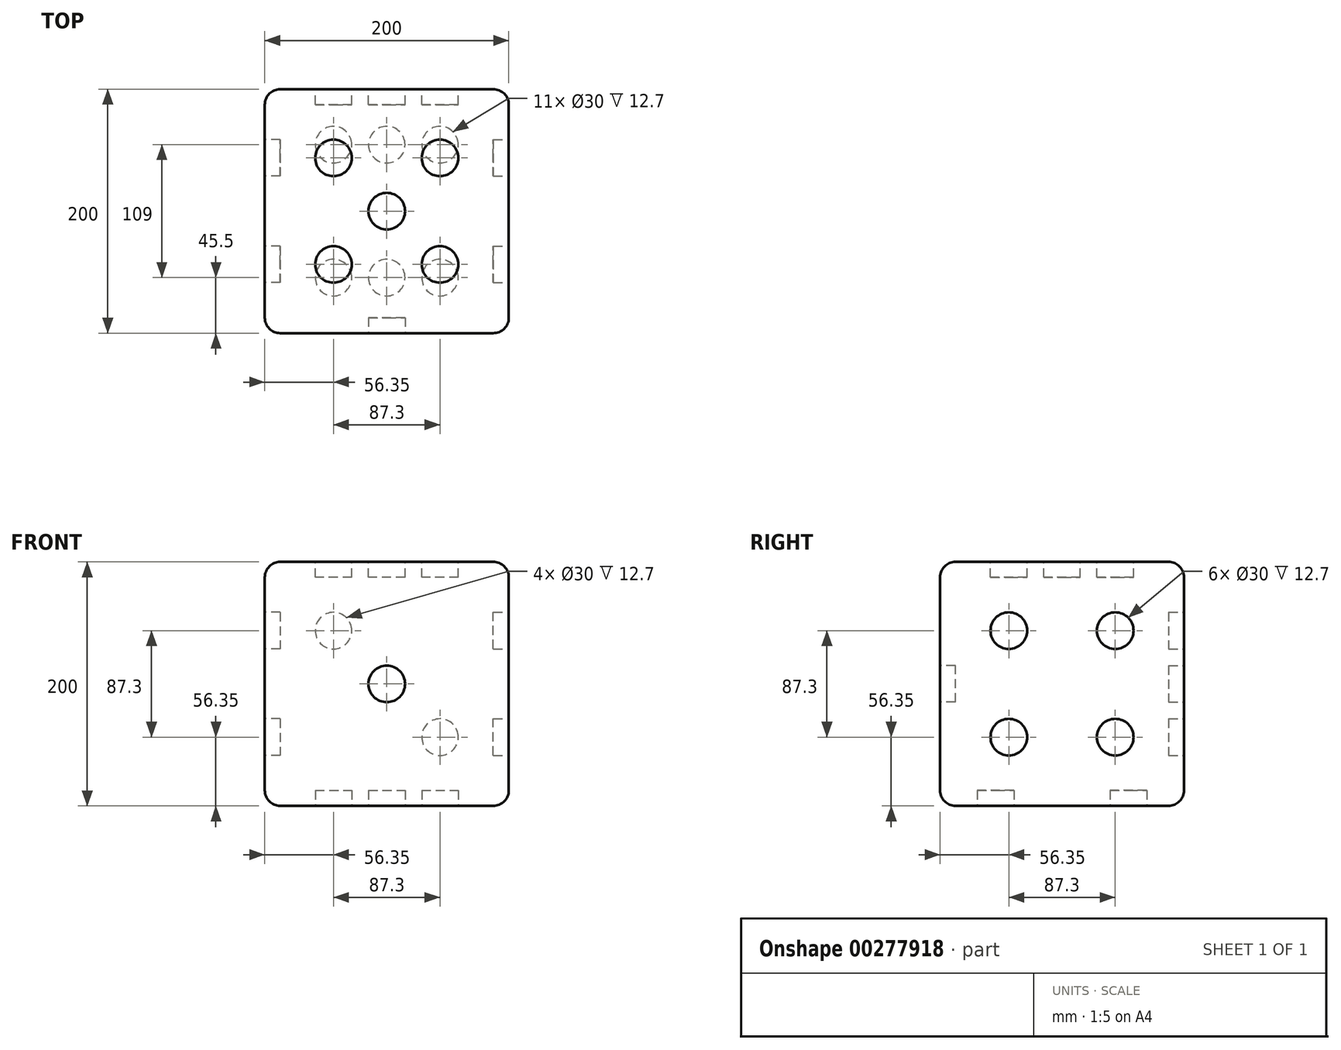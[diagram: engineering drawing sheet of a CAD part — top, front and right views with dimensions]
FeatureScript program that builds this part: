
annotation { "Feature Type Name" : "Feature", "Feature Type Description" : "" }
export const myFeature = defineFeature(function(context is Context, id is Id, definition is map)
    precondition{}
    {
        {
            var Q0;
            Q0=qCreatedBy(makeId("Front.planeOp"),FACE);
            var sketch = newSketch(context, id + "F0", { "sketchPlane" : qUnion([Q0])});
            skLineSegment(sketch, "E0.bottom", {"start": v(100, -100) * mm, "end": v(-100, -100) * mm});
            skLineSegment(sketch, "E0.top", {"start": v(100, 100) * mm, "end": v(-100, 100) * mm});
            skLineSegment(sketch, "E0.left", {"start": v(100, -100) * mm, "end": v(100, 100) * mm});
            skLineSegment(sketch, "E0.right", {"start": v(-100, -100) * mm, "end": v(-100, 100) * mm});
            skPoint(sketch, "E0.middle", {"position": v(0, 0) * mm});
            skSolve(sketch);
        }
        {
            var Q0;
            Q0 = qSketchRegion(id + "F0", true);
            extrude(context, id + "F1", {"entities" : qUnion([Q0]), "oppositeDirection" : true, "depth" : 200 * mm});
        }
        {
            var Q0;
            Q0=makeQuery(id+"F1.opExtrude","SWEPT_FACE",FACE,{"disambiguationData":[OSD([sQuery(id+"F0.wireOp",EDGE,"E0.top")])]});
            var Q1;
            Q1=makeQuery(id+"F1.opExtrude","SWEPT_FACE",FACE,{"disambiguationData":[OSD([sQuery(id+"F0.wireOp",EDGE,"E0.left")])]});
            var Q2;
            Q2=makeQuery(id+"F1.opExtrude","CAP_FACE",FACE,{"disambiguationData":[OSD([sQuery(id+"F0.wireOp",EDGE,"E0.bottom"),sQuery(id+"F0.wireOp",EDGE,"E0.top"),sQuery(id+"F0.wireOp",EDGE,"E0.left"),sQuery(id+"F0.wireOp",EDGE,"E0.right")])],"isStart":true});
            var Q3;
            Q3=makeQuery(id+"F1.opExtrude","SWEPT_FACE",FACE,{"disambiguationData":[OSD([sQuery(id+"F0.wireOp",EDGE,"E0.right")])]});
            var Q4;
            Q4=makeQuery(id+"F1.opExtrude","CAP_FACE",FACE,{"disambiguationData":[OSD([sQuery(id+"F0.wireOp",EDGE,"E0.bottom"),sQuery(id+"F0.wireOp",EDGE,"E0.top"),sQuery(id+"F0.wireOp",EDGE,"E0.left"),sQuery(id+"F0.wireOp",EDGE,"E0.right")])],"isStart":false});
            fillet(context, id + "F2", {"entities" : qUnion([Q0, Q1, Q2, Q3, Q4]), "radius" : 12.7 * mm, "tangentPropagation" : true, "allowEdgeOverflow" : false});
        }
        {
            var Q0;
            Q0=makeQuery(id+"F1.opExtrude","CAP_FACE",FACE,{"disambiguationData":[OSD([sQuery(id+"F0.wireOp",EDGE,"E0.bottom"),sQuery(id+"F0.wireOp",EDGE,"E0.top"),sQuery(id+"F0.wireOp",EDGE,"E0.left"),sQuery(id+"F0.wireOp",EDGE,"E0.right")])],"isStart":true});
            var sketch = newSketch(context, id + "F3", { "sketchPlane" : qUnion([Q0])});
            skCircle(sketch, "E1", {"center": v(0, 0) * mm, "radius": 15 * mm});
            skSolve(sketch);
        }
        {
            var Q0;
            Q0 = qSketchRegion(id + "F3", true);
            extrude(context, id + "F4", {"entities" : qUnion([Q0]), "operationType" : NewBodyOperationType.REMOVE, "oppositeDirection" : true, "depth" : 12.7 * mm});
        }
        {
            var Q0;
            Q0=makeQuery(id+"F1.opExtrude","SWEPT_FACE",FACE,{"disambiguationData":[OSD([sQuery(id+"F0.wireOp",EDGE,"E0.left")])]});
            var sketch = newSketch(context, id + "F5", { "sketchPlane" : qUnion([Q0])});
            skLineSegment(sketch, "E2", {"start": v(100, 87.3) * mm, "end": v(100, -87.3) * mm, "construction": true});
            skLineSegment(sketch, "E3", {"start": v(12.7, -87.3) * mm, "end": v(100, 0) * mm, "construction": true});
            skLineSegment(sketch, "E4", {"start": v(100, 0) * mm, "end": v(187.3, 87.3) * mm, "construction": true});
            skLineSegment(sketch, "E5", {"start": v(100, 0) * mm, "end": v(12.7, 87.3) * mm, "construction": true});
            skLineSegment(sketch, "E6", {"start": v(100, 0) * mm, "end": v(187.3, -87.3) * mm, "construction": true});
            skCircle(sketch, "E7", {"center": v(56.35, -43.65) * mm, "radius": 15 * mm});
            skCircle(sketch, "E8", {"center": v(143.65, -43.65) * mm, "radius": 15 * mm});
            skCircle(sketch, "E9", {"center": v(56.35, 43.65) * mm, "radius": 15 * mm});
            skCircle(sketch, "E10", {"center": v(143.65, 43.65) * mm, "radius": 15 * mm});
            skSolve(sketch);
        }
        {
            var Q0;
            Q0 = qSketchRegion(id + "F5", true);
            extrude(context, id + "F6", {"entities" : qUnion([Q0]), "operationType" : NewBodyOperationType.REMOVE, "oppositeDirection" : true, "depth" : 12.7 * mm});
        }
        {
            var Q0;
            Q0=makeQuery(id+"F1.opExtrude","SWEPT_FACE",FACE,{"disambiguationData":[OSD([sQuery(id+"F0.wireOp",EDGE,"E0.bottom")])]});
            var sketch = newSketch(context, id + "F7", { "sketchPlane" : qUnion([Q0])});
            skLineSegment(sketch, "E11", {"start": v(-87.3, -12.7) * mm, "end": v(0, -12.7) * mm, "construction": true});
            skLineSegment(sketch, "E12", {"start": v(0, -12.7) * mm, "end": v(0, -187.3) * mm, "construction": true});
            skLineSegment(sketch, "E13", {"start": v(0, -187.3) * mm, "end": v(-87.3, -187.3) * mm, "construction": true});
            skLineSegment(sketch, "E14", {"start": v(-87.3, -187.3) * mm, "end": v(-87.3, -12.7) * mm, "construction": true});
            skLineSegment(sketch, "E15", {"start": v(-43.65, -12.7) * mm, "end": v(-43.65, -187.3) * mm, "construction": true});
            skLineSegment(sketch, "E16", {"start": v(0, -12.7) * mm, "end": v(87.3, -12.7) * mm, "construction": true});
            skLineSegment(sketch, "E17", {"start": v(87.3, -12.7) * mm, "end": v(87.3, -187.3) * mm, "construction": true});
            skLineSegment(sketch, "E18", {"start": v(87.3, -187.3) * mm, "end": v(0, -187.3) * mm, "construction": true});
            skLineSegment(sketch, "E19", {"start": v(43.65, -12.7) * mm, "end": v(43.65, -187.3) * mm, "construction": true});
            skLineSegment(sketch, "E20", {"start": v(-87.3, -187.3) * mm, "end": v(-106.86, -187.3) * mm, "construction": true});
            skLineSegment(sketch, "E21", {"start": v(-106.86, -187.3) * mm, "end": v(-106.86, -154.5) * mm, "construction": true});
            skLineSegment(sketch, "E22", {"start": v(-106.86, -154.5) * mm, "end": v(-106.86, -45.5) * mm, "construction": true});
            skLineSegment(sketch, "E23", {"start": v(-106.86, -45.5) * mm, "end": v(-106.86, -12.7) * mm, "construction": true});
            skLineSegment(sketch, "E24", {"start": v(-106.86, -45.5) * mm, "end": v(87.3, -45.5) * mm, "construction": true});
            skLineSegment(sketch, "E25", {"start": v(-106.86, -154.5) * mm, "end": v(87.3, -154.5) * mm, "construction": true});
            skCircle(sketch, "E26", {"center": v(-43.65, -45.5) * mm, "radius": 15 * mm});
            skCircle(sketch, "E27", {"center": v(0, -45.5) * mm, "radius": 15 * mm});
            skCircle(sketch, "E28", {"center": v(43.65, -45.5) * mm, "radius": 15 * mm});
            skCircle(sketch, "E29", {"center": v(-43.65, -154.5) * mm, "radius": 15 * mm});
            skCircle(sketch, "E30", {"center": v(0, -154.5) * mm, "radius": 15 * mm});
            skCircle(sketch, "E31", {"center": v(43.65, -154.5) * mm, "radius": 15 * mm});
            skSolve(sketch);
        }
        {
            var Q0;
            Q0 = qSketchRegion(id + "F7", true);
            extrude(context, id + "F8", {"entities" : qUnion([Q0]), "operationType" : NewBodyOperationType.REMOVE, "oppositeDirection" : true, "depth" : 12.7 * mm});
        }
        {
            var Q0;
            Q0=makeQuery(id+"F1.opExtrude","SWEPT_FACE",FACE,{"disambiguationData":[OSD([sQuery(id+"F0.wireOp",EDGE,"E0.top")])]});
            var sketch = newSketch(context, id + "F9", { "sketchPlane" : qUnion([Q0])});
            skLineSegment(sketch, "E32", {"start": v(0, 187.3) * mm, "end": v(0, 12.7) * mm, "construction": true});
            skLineSegment(sketch, "E33", {"start": v(-87.3, 100) * mm, "end": v(87.3, 100) * mm, "construction": true});
            skLineSegment(sketch, "E34", {"start": v(-87.3, 12.7) * mm, "end": v(0, 12.7) * mm, "construction": true});
            skLineSegment(sketch, "E35", {"start": v(-43.65, 12.7) * mm, "end": v(-43.65, 100) * mm, "construction": true});
            skLineSegment(sketch, "E36", {"start": v(-43.65, 100) * mm, "end": v(-43.65, 187.3) * mm, "construction": true});
            skLineSegment(sketch, "E37", {"start": v(0, 12.7) * mm, "end": v(87.3, 12.7) * mm, "construction": true});
            skLineSegment(sketch, "E38", {"start": v(43.65, 12.7) * mm, "end": v(43.65, 100) * mm, "construction": true});
            skLineSegment(sketch, "E39", {"start": v(43.65, 100) * mm, "end": v(43.65, 187.3) * mm, "construction": true});
            skCircle(sketch, "E40", {"center": v(-43.65, 143.65) * mm, "radius": 15 * mm});
            skCircle(sketch, "E41", {"center": v(43.65, 143.65) * mm, "radius": 15 * mm});
            skCircle(sketch, "E42", {"center": v(-43.65, 56.35) * mm, "radius": 15 * mm});
            skCircle(sketch, "E43", {"center": v(43.65, 56.35) * mm, "radius": 15 * mm});
            skCircle(sketch, "E44", {"center": v(0, 100) * mm, "radius": 15 * mm});
            skSolve(sketch);
        }
        {
            var Q0;
            Q0 = qSketchRegion(id + "F9", true);
            extrude(context, id + "F10", {"entities" : qUnion([Q0]), "operationType" : NewBodyOperationType.REMOVE, "oppositeDirection" : true, "depth" : 12.7 * mm});
        }
        {
            var Q0;
            Q0=makeQuery(id+"F1.opExtrude","SWEPT_FACE",FACE,{"disambiguationData":[OSD([sQuery(id+"F0.wireOp",EDGE,"E0.right")])]});
            var sketch = newSketch(context, id + "F11", { "sketchPlane" : qUnion([Q0])});
            skLineSegment(sketch, "E45", {"start": v(-100, 87.3) * mm, "end": v(-100, -87.3) * mm, "construction": true});
            skLineSegment(sketch, "E46", {"start": v(-187.3, -87.3) * mm, "end": v(-100, 0) * mm, "construction": true});
            skLineSegment(sketch, "E47", {"start": v(-100, 0) * mm, "end": v(-12.7, 87.3) * mm, "construction": true});
            skCircle(sketch, "E48", {"center": v(-143.65, -43.65) * mm, "radius": 15 * mm});
            skCircle(sketch, "E49", {"center": v(-56.35, 43.65) * mm, "radius": 15 * mm});
            skSolve(sketch);
        }
        {
            var Q0;
            Q0 = qSketchRegion(id + "F11", true);
            extrude(context, id + "F12", {"entities" : qUnion([Q0]), "operationType" : NewBodyOperationType.REMOVE, "oppositeDirection" : true, "depth" : 12.7 * mm});
        }
        {
            var Q0;
            Q0=makeQuery(id+"F1.opExtrude","CAP_FACE",FACE,{"disambiguationData":[OSD([sQuery(id+"F0.wireOp",EDGE,"E0.bottom"),sQuery(id+"F0.wireOp",EDGE,"E0.top"),sQuery(id+"F0.wireOp",EDGE,"E0.left"),sQuery(id+"F0.wireOp",EDGE,"E0.right")])],"isStart":false});
            var sketch = newSketch(context, id + "F13", { "sketchPlane" : qUnion([Q0])});
            skLineSegment(sketch, "E50", {"start": v(0, 87.3) * mm, "end": v(0, -87.3) * mm, "construction": true});
            skLineSegment(sketch, "E51", {"start": v(-87.3, -87.3) * mm, "end": v(0, 0) * mm, "construction": true});
            skLineSegment(sketch, "E52", {"start": v(0, 0) * mm, "end": v(87.3, 87.3) * mm, "construction": true});
            skCircle(sketch, "E53", {"center": v(-43.65, -43.65) * mm, "radius": 15 * mm});
            skCircle(sketch, "E54", {"center": v(0, 0) * mm, "radius": 15 * mm});
            skCircle(sketch, "E55", {"center": v(43.65, 43.65) * mm, "radius": 15 * mm});
            skSolve(sketch);
        }
        {
            var Q0;
            Q0 = qSketchRegion(id + "F13", true);
            extrude(context, id + "F14", {"entities" : qUnion([Q0]), "operationType" : NewBodyOperationType.REMOVE, "oppositeDirection" : true, "depth" : 12.7 * mm});
        }
    });
